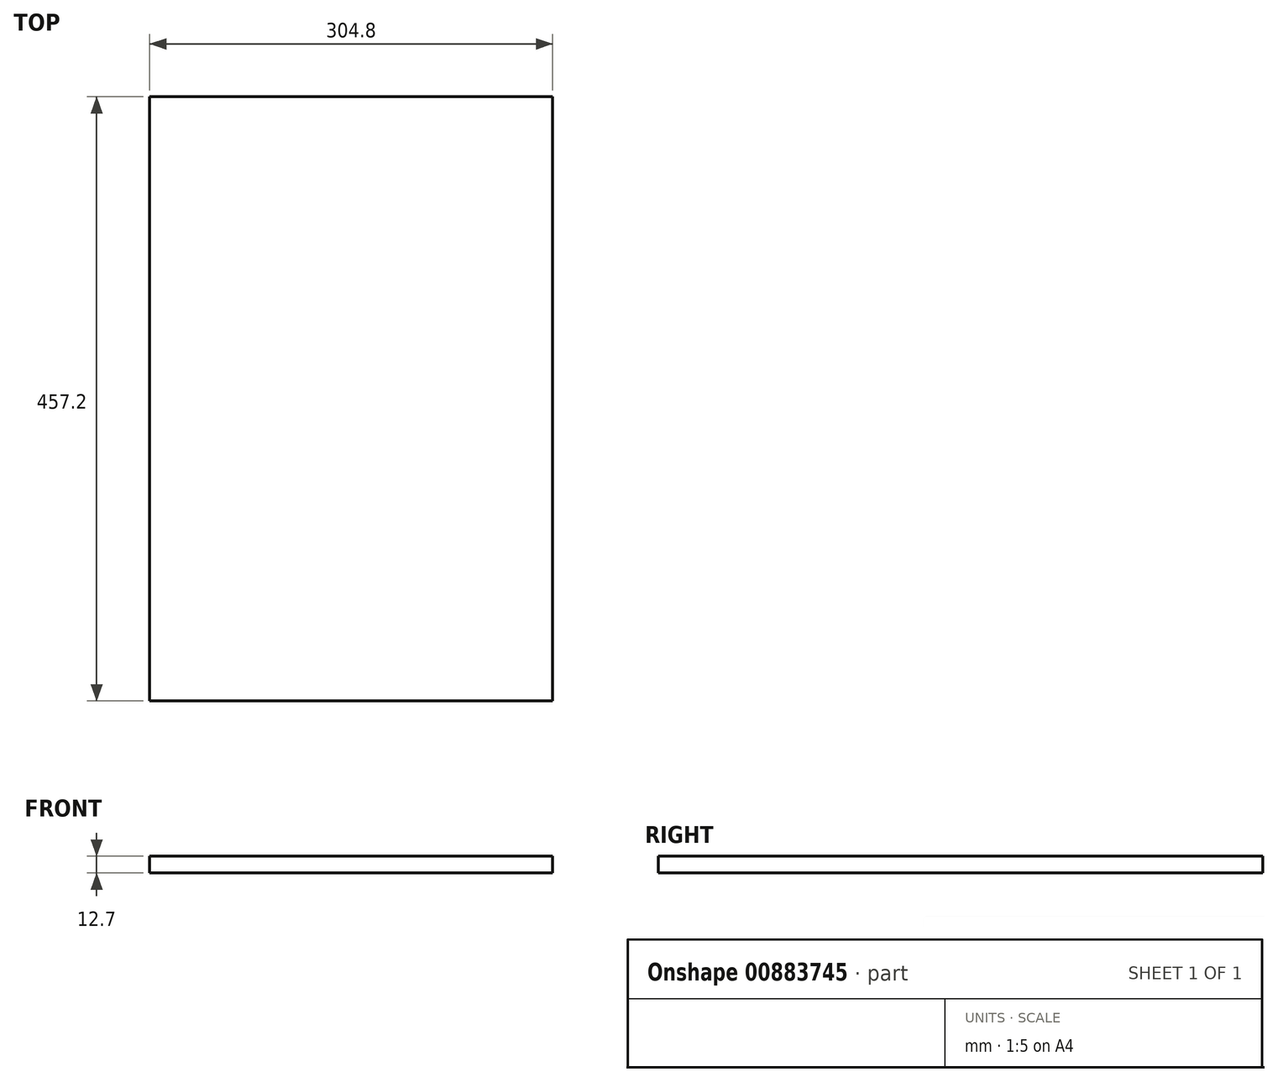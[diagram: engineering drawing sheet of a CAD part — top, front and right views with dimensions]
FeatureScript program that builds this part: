
annotation { "Feature Type Name" : "Feature", "Feature Type Description" : "" }
export const myFeature = defineFeature(function(context is Context, id is Id, definition is map)
    precondition{}
    {
        {
            var Q0;
            Q0=qCreatedBy(makeId("Top.planeOp"),FACE);
            var sketch = newSketch(context, id + "F0", { "sketchPlane" : qUnion([Q0])});
            skLineSegment(sketch, "E0.bottom", {"start": v(152.4, 228.6) * mm, "end": v(-152.4, 228.6) * mm});
            skLineSegment(sketch, "E0.top", {"start": v(152.4, -228.6) * mm, "end": v(-152.4, -228.6) * mm});
            skLineSegment(sketch, "E0.left", {"start": v(152.4, 228.6) * mm, "end": v(152.4, -228.6) * mm});
            skLineSegment(sketch, "E0.right", {"start": v(-152.4, 228.6) * mm, "end": v(-152.4, -228.6) * mm});
            skPoint(sketch, "E0.middle", {"position": v(0, 0) * mm});
            skSolve(sketch);
        }
        {
            var Q0;
            Q0=makeQuery(id+"F0.imprint","IMPRINT",FACE,{"disambiguationData":[TD([[makeQuery(id+"F0.imprint","IMPRINT",EDGE,{"derivedFrom":sQuery(id+"F0.wireOp",EDGE,"E0.bottom")}),1.0]])]});
            extrude(context, id + "F1", {"entities" : qUnion([Q0]), "depth" : 12.7 * mm, "offsetDistance" : 25.4 * mm});
        }
    });
